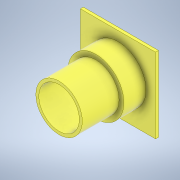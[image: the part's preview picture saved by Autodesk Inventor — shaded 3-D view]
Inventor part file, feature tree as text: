
AUTODESK INVENTOR PART (.ipt)
format: ipt  version: 2022.1 (Build 261234000, 234)  size: 961,024 bytes
history: native  units: mm
features: sketch x4, extrude x3, emboss x1
ambient origin geometry x8: Origin, YZ Plane, XZ Plane, XY Plane, X Axis, Y Axis, Z Axis, Center Point
bodies: Body1 (feature_tree)
feature tree (8):
  extrude  "Extrusion14"  Depth=51.0mm
  extrude  "Extrusion15"  Depth=2.0mm
  emboss  "Emboss3"
  extrude  "Extrusion16"  Depth=2.0mm
  sketch  "Sketch14"  dims[d74=51.0mm d75=51.0mm]
  sketch  "Sketch15"  dims[d76=27.496mm d77=2.0mm]
  sketch  "Sketch16"  dims[d78=0.0mm d79=2.0mm]
  sketch  "Sketch22"  dims[d80=40.0mm d81=0.0mm d82=5.0mm d83=1.0mm d84=0.0mm d105=38.0mm d106=15.0mm d107=0.0mm]
